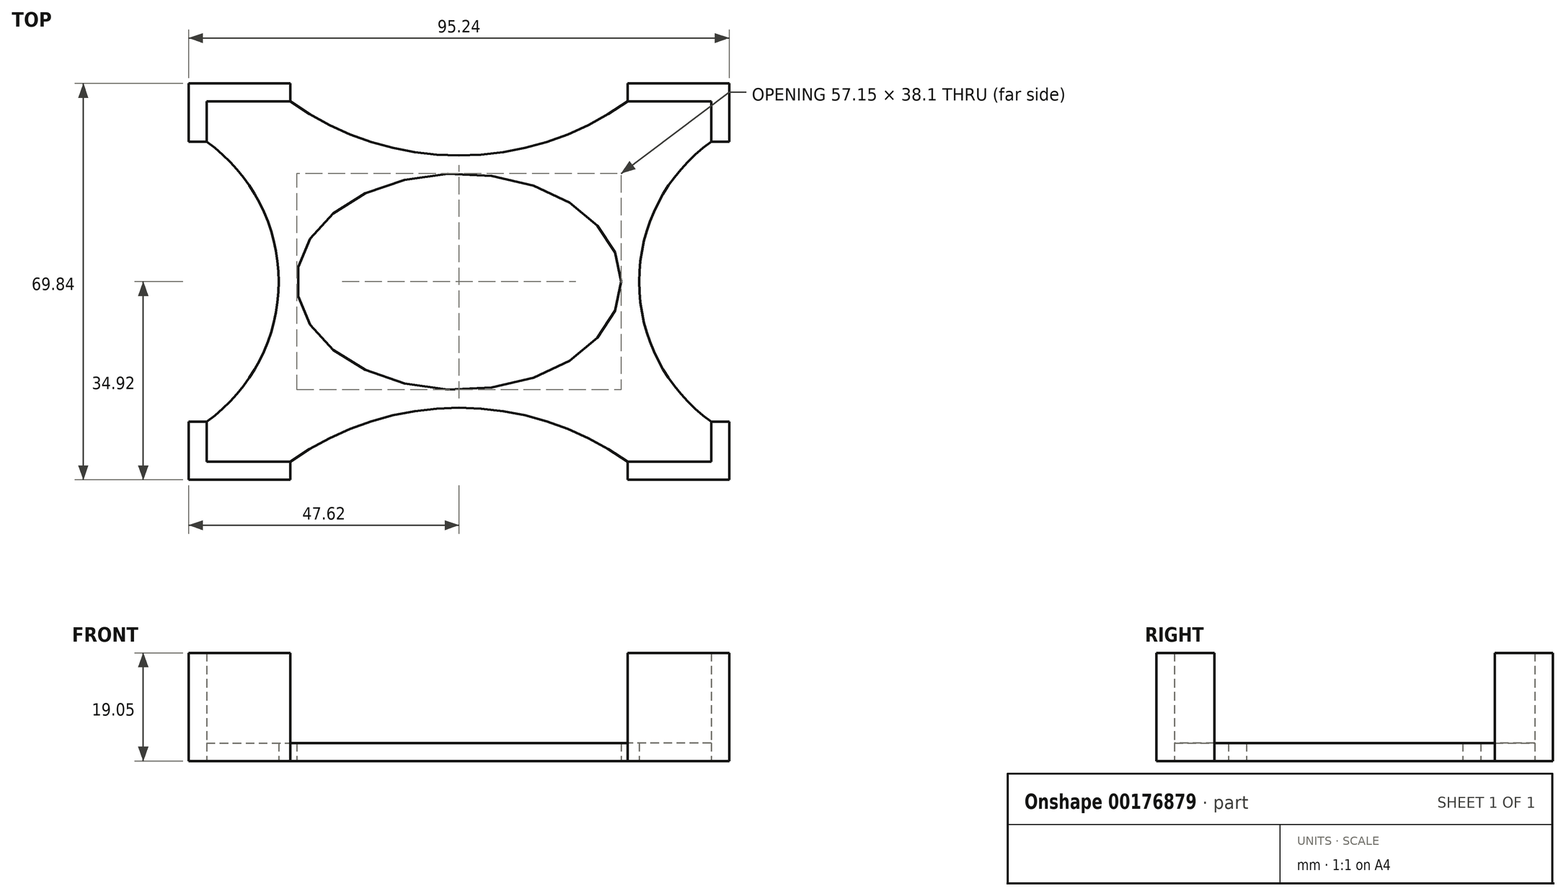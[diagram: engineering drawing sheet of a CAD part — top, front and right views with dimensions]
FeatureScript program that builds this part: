
annotation { "Feature Type Name" : "Feature", "Feature Type Description" : "" }
export const myFeature = defineFeature(function(context is Context, id is Id, definition is map)
    precondition{}
    {
        {
            var Q0;
            Q0=qCreatedBy(makeId("Top.planeOp"),FACE);
            var sketch = newSketch(context, id + "F0", { "sketchPlane" : qUnion([Q0])});
            skLineSegment(sketch, "E0.bottom", {"start": v(44.45, 31.75) * mm, "end": v(-44.45, 31.75) * mm, "construction": true});
            skLineSegment(sketch, "E0.top", {"start": v(44.45, -31.75) * mm, "end": v(-44.45, -31.75) * mm, "construction": true});
            skLineSegment(sketch, "E0.left", {"start": v(44.45, 31.75) * mm, "end": v(44.45, -31.75) * mm, "construction": true});
            skLineSegment(sketch, "E0.right", {"start": v(-44.45, 31.75) * mm, "end": v(-44.45, -31.75) * mm, "construction": true});
            skPoint(sketch, "E0.middle", {"position": v(0, 0) * mm});
            skLineSegment(sketch, "E1", {"start": v(-44.45, -31.75) * mm, "end": v(44.45, 31.75) * mm, "construction": true});
            skLineSegment(sketch, "E2", {"start": v(-44.45, 31.75) * mm, "end": v(44.45, -31.75) * mm, "construction": true});
            skLineSegment(sketch, "E3", {"start": v(-44.45, 0) * mm, "end": v(44.45, 0) * mm, "construction": true});
            skLineSegment(sketch, "E4", {"start": v(0, 31.75) * mm, "end": v(0, -31.75) * mm, "construction": true});
            skLineSegment(sketch, "E5", {"start": v(-44.45, 24.68) * mm, "end": v(-44.45, 31.75) * mm});
            skLineSegment(sketch, "E6", {"start": v(-44.45, 31.75) * mm, "end": v(-29.72, 31.75) * mm});
            skArc(sketch, "E7", {"start": v(-29.72, 31.75) * mm, "mid": v(0, 22.23) * mm, "end": v(29.72, 31.75) * mm});
            skLineSegment(sketch, "E8.MirrorCS", {"start": v(44.45, 31.75) * mm, "end": v(29.72, 31.75) * mm});
            skLineSegment(sketch, "E9.MirrorCS", {"start": v(44.45, 24.68) * mm, "end": v(44.45, 31.75) * mm});
            skEllipse(sketch, "E10", {"center": v(0, 0) * mm, "majorRadius": 22.23 * mm, "minorRadius": 31.75 * mm, "majorAxis": v(0, 1), "construction": true});
            skEllipse(sketch, "E11", {"center": v(0, 0) * mm, "majorRadius": 28.58 * mm, "minorRadius": 19.05 * mm, "majorAxis": v(1, 0)});
            skLineSegment(sketch, "E12", {"start": v(0, 10.52) * mm, "end": v(-29.72, 31.75) * mm, "construction": true});
            skArc(sketch, "E13", {"start": v(-44.45, -24.68) * mm, "mid": v(-31.75, 0) * mm, "end": v(-44.45, 24.68) * mm});
            skLineSegment(sketch, "E14.MirrorCS", {"start": v(-44.45, -24.68) * mm, "end": v(-44.45, -31.75) * mm});
            skLineSegment(sketch, "E15.MirrorCS", {"start": v(-44.45, -31.75) * mm, "end": v(-29.72, -31.75) * mm});
            skArc(sketch, "E16.MirrorCS", {"start": v(-29.72, -31.75) * mm, "mid": v(0, -22.23) * mm, "end": v(29.72, -31.75) * mm});
            skLineSegment(sketch, "E17.MirrorCS", {"start": v(44.45, -31.75) * mm, "end": v(29.72, -31.75) * mm});
            skLineSegment(sketch, "E18.MirrorCS", {"start": v(44.45, -24.68) * mm, "end": v(44.45, -31.75) * mm});
            skArc(sketch, "E19.MirrorCS", {"start": v(44.45, -24.68) * mm, "mid": v(31.75, 0) * mm, "end": v(44.45, 24.68) * mm});
            skLineSegment(sketch, "E20", {"start": v(-44.45, 24.68) * mm, "end": v(-26.71, 12.01) * mm, "construction": true});
            skSolve(sketch);
        }
        {
            var Q0;
            Q0 = qSketchRegion(id + "F0", true);
            extrude(context, id + "F1", {"entities" : qUnion([Q0]), "depth" : 3.17 * mm});
        }
        {
            var Q0;
            Q0=qCreatedBy(makeId("Top.planeOp"),FACE);
            var sketch = newSketch(context, id + "F2", { "sketchPlane" : qUnion([Q0])});
            skLineSegment(sketch, "E21", {"start": v(0, 0) * mm, "end": v(62.85, 0) * mm, "construction": true});
            skLineSegment(sketch, "E22", {"start": v(0, 0) * mm, "end": v(0, 39.52) * mm, "construction": true});
            skLineSegment(sketch, "E23", {"start": v(-44.45, 24.68) * mm, "end": v(-47.62, 24.68) * mm});
            skLineSegment(sketch, "E24", {"start": v(-47.62, 24.68) * mm, "end": v(-47.62, 34.93) * mm});
            skLineSegment(sketch, "E25", {"start": v(-47.62, 34.92) * mm, "end": v(-29.72, 34.92) * mm});
            skLineSegment(sketch, "E26", {"start": v(-29.72, 34.92) * mm, "end": v(-29.72, 31.75) * mm});
            skLineSegment(sketch, "E27", {"start": v(-44.45, 24.68) * mm, "end": v(-44.45, 31.75) * mm});
            skLineSegment(sketch, "E28", {"start": v(-44.45, 31.75) * mm, "end": v(-29.72, 31.75) * mm});
            skLineSegment(sketch, "E29.MirrorCS", {"start": v(44.45, 31.75) * mm, "end": v(29.72, 31.75) * mm});
            skLineSegment(sketch, "E30.MirrorCS", {"start": v(44.45, 24.68) * mm, "end": v(44.45, 31.75) * mm});
            skLineSegment(sketch, "E31.MirrorCS", {"start": v(44.45, 24.68) * mm, "end": v(47.62, 24.68) * mm});
            skLineSegment(sketch, "E32.MirrorCS", {"start": v(47.62, 24.68) * mm, "end": v(47.62, 34.93) * mm});
            skLineSegment(sketch, "E33.MirrorCS", {"start": v(47.62, 34.92) * mm, "end": v(29.72, 34.92) * mm});
            skLineSegment(sketch, "E34.MirrorCS", {"start": v(29.72, 34.92) * mm, "end": v(29.72, 31.75) * mm});
            skLineSegment(sketch, "E35.MirrorCS", {"start": v(-44.45, -24.68) * mm, "end": v(-47.62, -24.68) * mm});
            skLineSegment(sketch, "E36.MirrorCS", {"start": v(-47.62, -24.68) * mm, "end": v(-47.62, -34.93) * mm});
            skLineSegment(sketch, "E37.MirrorCS", {"start": v(44.45, -24.68) * mm, "end": v(47.62, -24.68) * mm});
            skLineSegment(sketch, "E38.MirrorCS", {"start": v(44.45, -31.75) * mm, "end": v(29.72, -31.75) * mm});
            skLineSegment(sketch, "E39.MirrorCS", {"start": v(44.45, -24.68) * mm, "end": v(44.45, -31.75) * mm});
            skLineSegment(sketch, "E40.MirrorCS", {"start": v(29.72, -34.92) * mm, "end": v(29.72, -31.75) * mm});
            skLineSegment(sketch, "E41.MirrorCS", {"start": v(47.62, -24.68) * mm, "end": v(47.62, -34.93) * mm});
            skLineSegment(sketch, "E42.MirrorCS", {"start": v(-47.62, -34.93) * mm, "end": v(-29.72, -34.93) * mm});
            skLineSegment(sketch, "E43.MirrorCS", {"start": v(-44.45, -24.68) * mm, "end": v(-44.45, -31.75) * mm});
            skLineSegment(sketch, "E44.MirrorCS", {"start": v(-29.72, -34.92) * mm, "end": v(-29.72, -31.75) * mm});
            skLineSegment(sketch, "E45.MirrorCS", {"start": v(47.62, -34.92) * mm, "end": v(29.72, -34.92) * mm});
            skLineSegment(sketch, "E46.MirrorCS", {"start": v(-44.45, -31.75) * mm, "end": v(-29.72, -31.75) * mm});
            skSolve(sketch);
        }
        {
            var Q0;
            Q0 = qSketchRegion(id + "F2", true);
            extrude(context, id + "F3", {"entities" : qUnion([Q0]), "operationType" : NewBodyOperationType.ADD, "depth" : 19.05 * mm});
        }
    });
